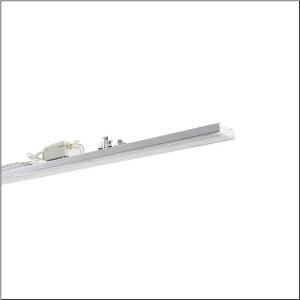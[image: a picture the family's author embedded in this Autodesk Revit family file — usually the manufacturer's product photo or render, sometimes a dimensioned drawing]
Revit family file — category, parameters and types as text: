
# Revit family: licross_11_recessed_mo_51te10cn49xg
name_source: partatom
category: Lighting Fixtures
units: mm (PartAtom-declared; Revit-internal decimal feet)

## family parameters
Cut with Voids When Loaded = No
Host = Face
Light Source = No
Part Type = Normal
Room Calculation Point = No
Round Connector Dimension = Use Diameter
Shared = No

## types (1)
- --- (1 x LED, 9050 lm, 49.3 W, 4000K)
    Apparent Load = 49 VA
    CIE Flux Codes = 50 81 96 100 100
    Color Rendering = 80
    Color Temperature = 4000K
    Default Elevation = 1800 mm
    Description = Licross 11 Recessed MO, luminaire insert, of sheet steel, galvanised, coil coated, white, length: 1.500mm, width: 66mm, height: 67mm, LED rated luminous flux: 9.050lm, light colour: 840, SDCM (Standard Deviation of Colour Matching)MacAdam ≤ 2 SDCM (initial), control gear: ON/OFF Multilumen, CLOi, with plug, 3-pole, with phase selection, mains connection: 220..240V, AC, 50/60Hz, start of lifetime: 49W, end of service life: 55W, internal wiring halogen-free, primary optical cover: cover, of PMMA, light emission: direct distribution, primary light characteristic: symmetric, protection rating (complete): IP54, insulation class (complete): insulation class I (protective earthing), certification: CE, ENEC, VDE, UKCA, protection symbol: D if used in an environment with non-conductive dust loads with corresponding accessories, impact resistance: IK06, permissible ambient temperature for indoor applications: -35..+40°C, corresponds to IFS (International Featured Standards) requirements for safety and quality in the food industry, reducing of maximum allowable ambient temperature of 5°C with ceiling mounting, LABS conformity tested according to VDMA 24364:2018-05, The light source and the operating device comply with the requirements of the Ecodesign Regulation (EU) 2019/2020 and are replaceable in accordance with this regulation, packaging unit: 1 piece
    Height = 58 mm
    Lamp = 1 x LED
    Lamp Light Flux = 9050 lm
    Lamp Power = 49.3 W
    Lamp count = 1
    Length = 1500 mm
    Luminous efficacy = 184 lm/W
    Manufacturer = Siteco
    ModVariant = No
    Model = 51TE10CN49XG
    Mounting Place = Ceiling
    Mounting Type = Pendant
    Number of Poles = 1
    OnlyDefault = Yes
    Power Factor = 1
    Product Name = Licross 11 Recessed MO
    Product group = luminaire insert | ceiling pendant
    ProductGroupID = 901
    Protection Class = Protection class I
    Protection Degree = IP 54
    RLX_Detail_Level = 1
    RLX_Emergency_Light_Flux = 0 lm
    RLX_Emergency_Type = 0
    RLX_Emergency_Type_DB = No
    RlxData = <blob elided: 22429 chars, md5=ac286c65>
    Socket = socket
    Standby Power = 0 W
    System Light Flux = 9050 lm
    System Power = 49 W
    Type Comments = factory setting: luminous flux: 100 % | (A | C | E) | 113 mA
    Type Image = l_1296930.jpg
    URL = http://relux.com
    VarID = @adj_000421
    Voltage = 0 V
    Weight = 0.00 kg
    Width = 66 mm

## geometry (parser evidence)
native form markers: Blend x4, Sweep x9
no freeform markers — native parametric forms only
